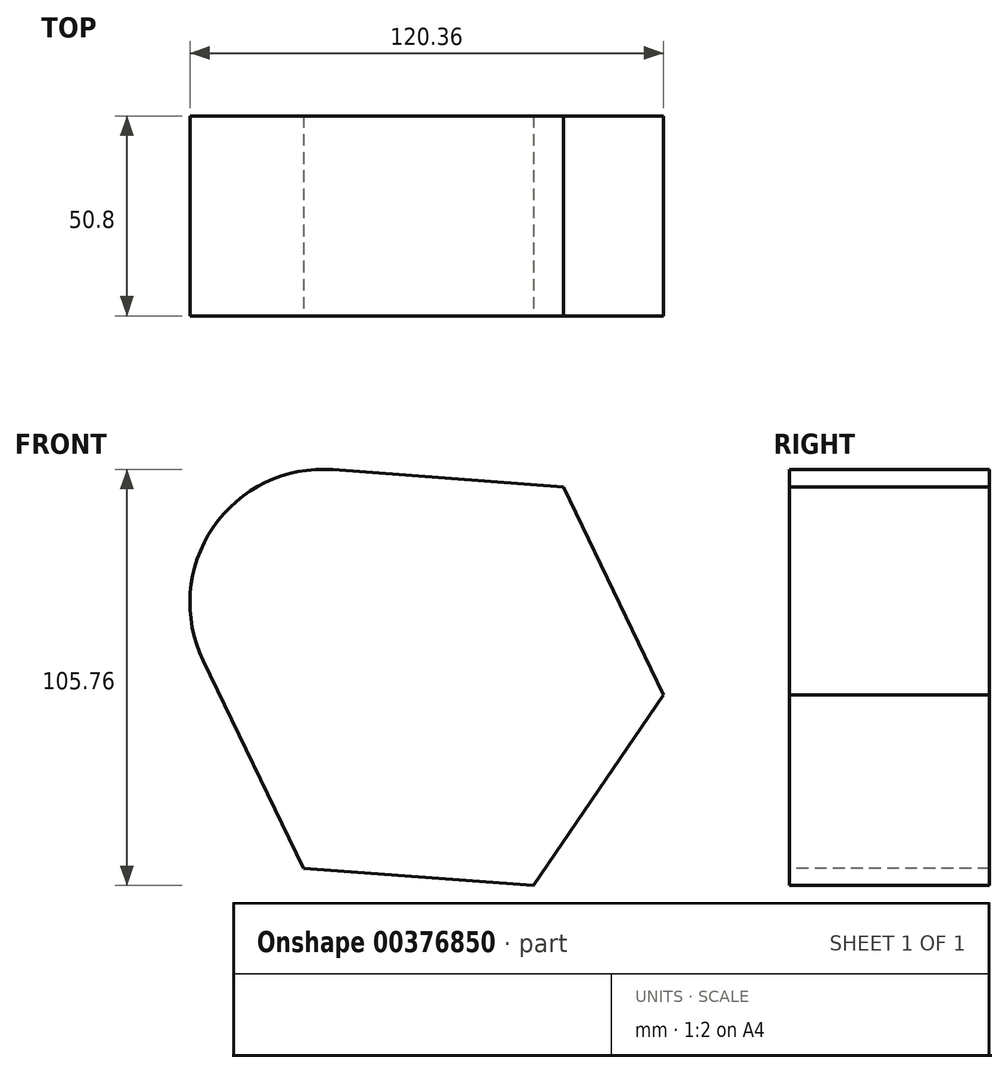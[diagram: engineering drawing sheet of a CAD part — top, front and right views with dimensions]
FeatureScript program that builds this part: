
annotation { "Feature Type Name" : "Feature", "Feature Type Description" : "" }
export const myFeature = defineFeature(function(context is Context, id is Id, definition is map)
    precondition{}
    {
        {
            var Q0;
            Q0=qCreatedBy(makeId("Front.planeOp"),FACE);
            var sketch = newSketch(context, id + "F0", { "sketchPlane" : qUnion([Q0])});
            skCircle(sketch, "E0.cCircle", {"center": v(-27.96, 0) * mm, "radius": 50.8 * mm, "construction": true});
            skLineSegment(sketch, "E0.0", {"start": v(-60.97, -48.49) * mm, "end": v(-86.45, 4.34) * mm});
            skLineSegment(sketch, "E0.2", {"start": v(-53.44, 52.83) * mm, "end": v(5.05, 48.49) * mm});
            skLineSegment(sketch, "E0.3", {"start": v(5.05, 48.49) * mm, "end": v(30.54, -4.34) * mm});
            skLineSegment(sketch, "E0.4", {"start": v(30.54, -4.34) * mm, "end": v(-2.47, -52.83) * mm});
            skLineSegment(sketch, "E0.5", {"start": v(-2.47, -52.83) * mm, "end": v(-60.97, -48.49) * mm});
            skPoint(sketch, "E0.0.midPoint", {"position": v(-73.71, -22.07) * mm});
            skArc(sketch, "E1.converted", {"start": v(-53.44, 52.83) * mm, "mid": v(-83.95, 38.12) * mm, "end": v(-86.45, 4.34) * mm});
            skSolve(sketch);
        }
        {
            var Q0;
            Q0=makeQuery(id+"F0.imprint","IMPRINT",FACE,{"disambiguationData":[TD([[makeQuery(id+"F0.imprint","IMPRINT",EDGE,{"derivedFrom":sQuery(id+"F0.wireOp",EDGE,"E0.0")}),-1.0]])]});
            extrude(context, id + "F1", {"entities" : qUnion([Q0]), "oppositeDirection" : true, "depth" : 50.8 * mm});
        }
    });
